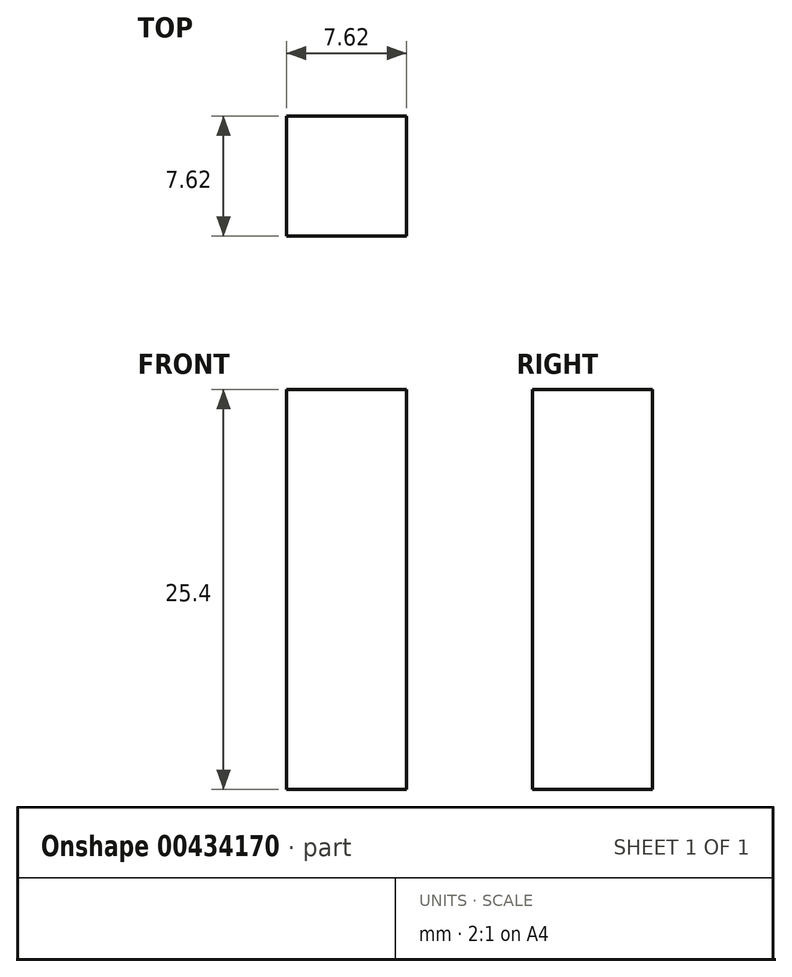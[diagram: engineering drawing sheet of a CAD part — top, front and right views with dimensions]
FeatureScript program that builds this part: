
annotation { "Feature Type Name" : "Feature", "Feature Type Description" : "" }
export const myFeature = defineFeature(function(context is Context, id is Id, definition is map)
    precondition{}
    {
        {
            var Q0;
            Q0=qCreatedBy(makeId("Front.planeOp"),FACE);
            var sketch = newSketch(context, id + "F0", { "sketchPlane" : qUnion([Q0])});
            skLineSegment(sketch, "E0.bottom", {"start": v(-3.81, 12.7) * mm, "end": v(3.8, 12.7) * mm});
            skLineSegment(sketch, "E0.top", {"start": v(-3.8, -12.7) * mm, "end": v(3.81, -12.7) * mm});
            skLineSegment(sketch, "E0.left", {"start": v(-3.81, 12.7) * mm, "end": v(-3.8, -12.7) * mm});
            skLineSegment(sketch, "E0.right", {"start": v(3.8, 12.7) * mm, "end": v(3.81, -12.7) * mm});
            skPoint(sketch, "E0.middle", {"position": v(0, 0) * mm});
            skSolve(sketch);
        }
        {
            var Q0;
            Q0=makeQuery(id+"F0.imprint","IMPRINT",FACE,{"disambiguationData":[TD([[makeQuery(id+"F0.imprint","IMPRINT",EDGE,{"derivedFrom":sQuery(id+"F0.wireOp",EDGE,"E0.bottom")}),-1.0]])]});
            extrude(context, id + "F1", {"entities" : qUnion([Q0]), "depth" : 7.62 * mm});
        }
    });
